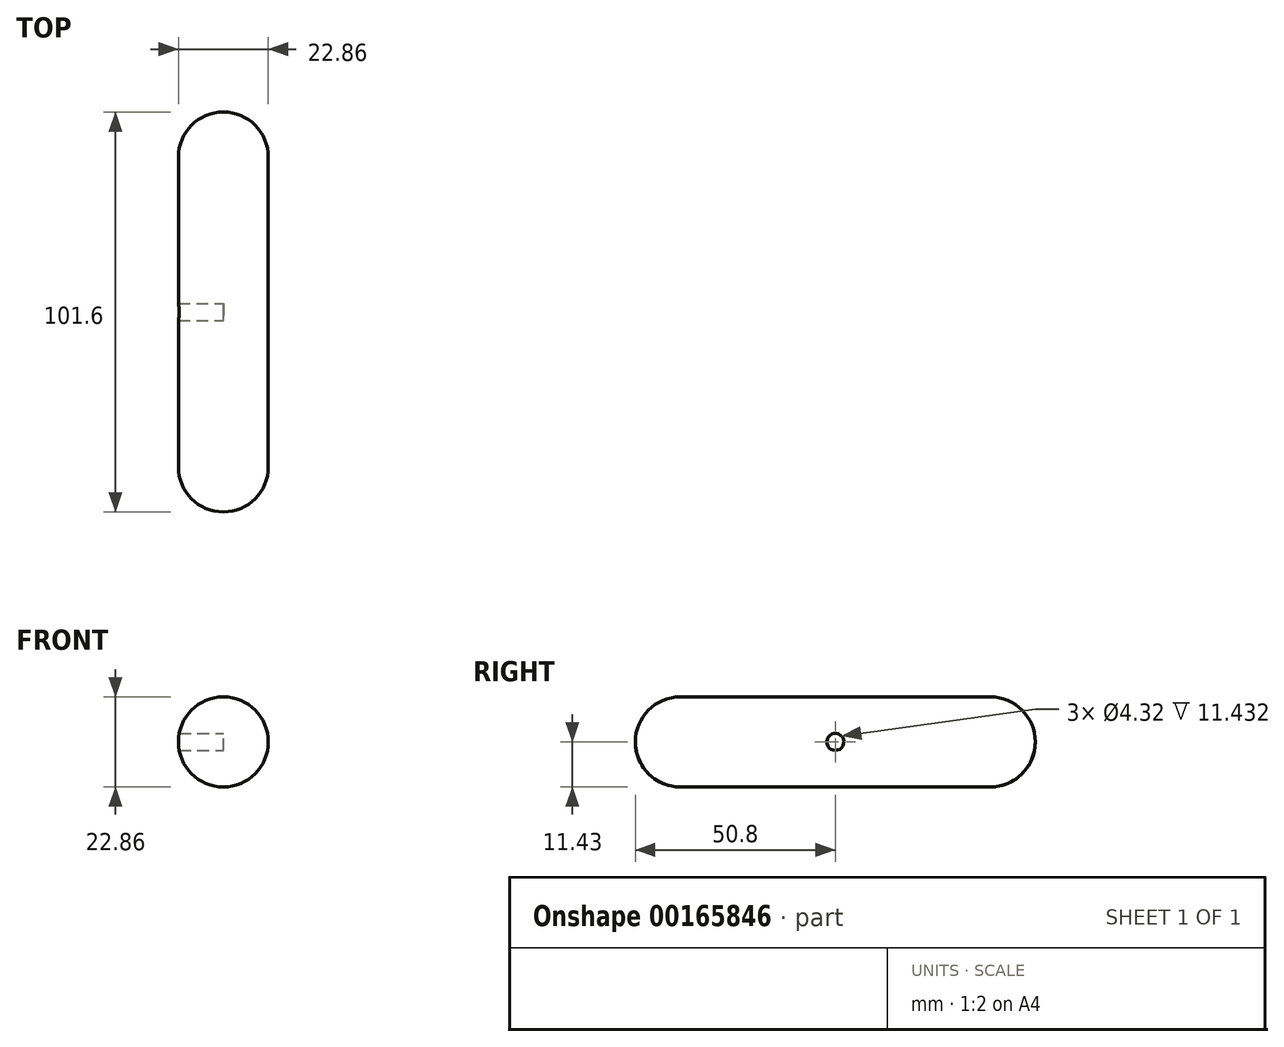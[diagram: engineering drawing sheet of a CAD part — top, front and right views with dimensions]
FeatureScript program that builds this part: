
annotation { "Feature Type Name" : "Feature", "Feature Type Description" : "" }
export const myFeature = defineFeature(function(context is Context, id is Id, definition is map)
    precondition{}
    {
        {
            var Q0;
            Q0=qCreatedBy(makeId("Front.planeOp"),FACE);
            var sketch = newSketch(context, id + "F0", { "sketchPlane" : qUnion([Q0])});
            skCircle(sketch, "E0", {"center": v(0, 0) * mm, "radius": 11.43 * mm});
            skSolve(sketch);
        }
        {
            var Q0;
            Q0=makeQuery(id+"F0.imprint","IMPRINT",FACE,{"disambiguationData":[TD([[makeQuery(id+"F0.imprint","IMPRINT",EDGE,{"derivedFrom":sQuery(id+"F0.wireOp",EDGE,"E0")}),1.0]])]});
            extrude(context, id + "F1", {"entities" : qUnion([Q0]), "endBound" : BoundingType.SYMMETRIC, "depth" : 101.6 * mm});
        }
        {
            var Q0;
            Q0=makeQuery(id+"F1.opExtrude","CAP_EDGE",EDGE,{"disambiguationData":[OSD([sQuery(id+"F0.wireOp",EDGE,"E0")])],"isStart":true});
            var Q1;
            Q1=makeQuery(id+"F1.opExtrude","CAP_EDGE",EDGE,{"disambiguationData":[OSD([sQuery(id+"F0.wireOp",EDGE,"E0")])],"isStart":false});
            fillet(context, id + "F2", {"entities" : qUnion([Q0, Q1]), "radius" : 11.43 * mm, "tangentPropagation" : true, "allowEdgeOverflow" : false});
        }
        {
            var Q0;
            Q0=qCreatedBy(makeId("Right.planeOp"),FACE);
            var sketch = newSketch(context, id + "F3", { "sketchPlane" : qUnion([Q0])});
            skLineSegment(sketch, "E1.0", {"start": v(0, -11.43) * mm, "end": v(0, 11.43) * mm});
            skPoint(sketch, "E2", {"position": v(0, 0) * mm});
            skSolve(sketch);
        }
        {
            var Q0;
            Q0=sQuery(id+"F3.wireOp",VERTEX,"E2");
            var Q1;
            Q1=makeQuery(id+"F1.opExtrude","SWEPT_BODY",BODY,{"disambiguationData":[OSD([sQuery(id+"F0.wireOp",EDGE,"E0")])]});
            hole(context, id + "F4", {"style" : HoleStyle.SIMPLE, "endStyle" : HoleEndStyle.THROUGH, "holeDiameter" : 4.32 * mm, "startFromSketch" : true, "locations" : qUnion([Q0]), "scope" : qUnion([Q1]), "isTappedThrough" : true});
        }
    });
